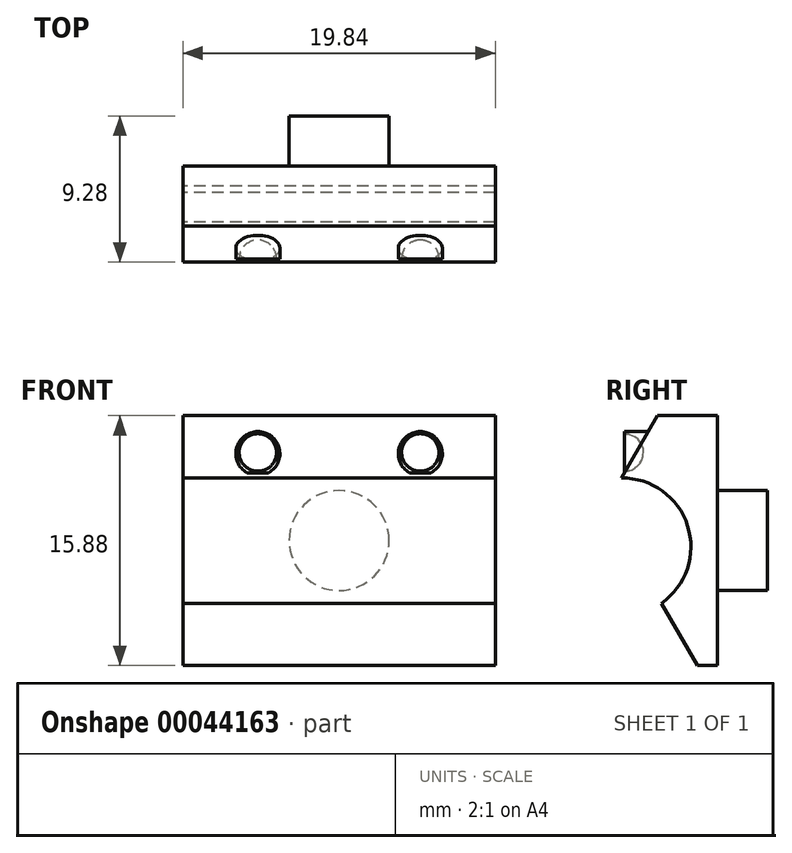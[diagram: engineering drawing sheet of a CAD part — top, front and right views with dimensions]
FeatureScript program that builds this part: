
annotation { "Feature Type Name" : "Feature", "Feature Type Description" : "" }
export const myFeature = defineFeature(function(context is Context, id is Id, definition is map)
    precondition{}
    {
        {
            var Q0;
            Q0=qCreatedBy(makeId("Right.planeOp"),FACE);
            var sketch = newSketch(context, id + "F0", { "sketchPlane" : qUnion([Q0])});
            skLineSegment(sketch, "E0", {"start": v(0, 0) * mm, "end": v(-1.27, 0) * mm});
            skLineSegment(sketch, "E1", {"start": v(-1.27, 0) * mm, "end": v(-3.56, 3.96) * mm});
            skArc(sketch, "E2", {"start": v(-3.56, 3.96) * mm, "mid": v(-1.88, 8.88) * mm, "end": v(-6.1, 11.92) * mm});
            skLineSegment(sketch, "E3", {"start": v(0, 15.88) * mm, "end": v(-3.81, 15.88) * mm});
            skLineSegment(sketch, "E4", {"start": v(-3.81, 15.88) * mm, "end": v(-6.1, 11.92) * mm});
            skLineSegment(sketch, "E5", {"start": v(0, 0) * mm, "end": v(0, 15.88) * mm});
            skSolve(sketch);
        }
        {
            var Q0;
            Q0=makeQuery(id+"F0.imprint","IMPRINT",FACE,{"disambiguationData":[TD([[makeQuery(id+"F0.imprint","IMPRINT",EDGE,{"derivedFrom":sQuery(id+"F0.wireOp",EDGE,"E0")}),-1.0]])]});
            extrude(context, id + "F1", {"entities" : qUnion([Q0]), "depth" : 19.84 * mm});
        }
        {
            var Q0;
            Q0=qCreatedBy(makeId("Front.planeOp"),FACE);
            cPlane(context, id + "F2", {"entities" : qUnion([Q0]), "cplaneType" : CPlaneType.OFFSET, "offset" : 4.32 * mm, "width" : 152.4 * mm, "height" : 152.4 * mm});
        }
        {
            var Q0;
            Q0=qCreatedBy(id+"F2.planeOp",FACE);
            var sketch = newSketch(context, id + "F3", { "sketchPlane" : qUnion([Q0])});
            skCircle(sketch, "E6", {"center": v(4.76, 13.46) * mm, "radius": 1.4 * mm});
            skCircle(sketch, "E7", {"center": v(15.08, 13.46) * mm, "radius": 1.4 * mm});
            skLineSegment(sketch, "E8", {"start": v(0, 13.46) * mm, "end": v(4.76, 13.46) * mm});
            skLineSegment(sketch, "E9", {"start": v(15.08, 13.46) * mm, "end": v(4.76, 13.46) * mm});
            skSolve(sketch);
        }
        {
            var Q0;
            Q0=makeQuery(id+"F3.imprint","IMPRINT",FACE,{"disambiguationData":[TD([[makeQuery(id+"F3.imprint","IMPRINT",EDGE,{"derivedFrom":sQuery(id+"F3.wireOp",EDGE,"E6")}),1.0]])]});
            var Q1;
            Q1=makeQuery(id+"F3.imprint","IMPRINT",FACE,{"disambiguationData":[TD([[makeQuery(id+"F3.imprint","IMPRINT",EDGE,{"derivedFrom":sQuery(id+"F3.wireOp",EDGE,"E7")}),1.0]])]});
            extrude(context, id + "F4", {"entities" : qUnion([Q0, Q1]), "operationType" : NewBodyOperationType.ADD, "depth" : 1.59 * mm});
        }
        {
            var Q0;
            Q0=qCreatedBy(makeId("Right.planeOp"),FACE);
            cPlane(context, id + "F5", {"entities" : qUnion([Q0]), "cplaneType" : CPlaneType.OFFSET, "offset" : 4.76 * mm, "width" : 152.4 * mm, "height" : 152.4 * mm});
        }
        {
            var Q0;
            Q0=qCreatedBy(id+"F5.planeOp",FACE);
            var sketch = newSketch(context, id + "F6", { "sketchPlane" : qUnion([Q0])});
            skLineSegment(sketch, "E10", {"start": v(-5.9, 12.34) * mm, "end": v(-5.9, 13.54) * mm});
            skArc(sketch, "E11", {"start": v(-5.9, 12.34) * mm, "mid": v(-4.7, 13.54) * mm, "end": v(-5.9, 14.73) * mm});
            skLineSegment(sketch, "E12", {"start": v(-5.9, 13.54) * mm, "end": v(-5.9, 14.88) * mm});
            skLineSegment(sketch, "E13", {"start": v(0, 0) * mm, "end": v(-5.9, 0) * mm});
            skLineSegment(sketch, "E14", {"start": v(-5.9, 0) * mm, "end": v(-5.9, 12.34) * mm});
            skSolve(sketch);
        }
        {
            var Q0;
            Q0 = qSketchRegion(id + "F6", true);
            var Q1;
            Q1=sQuery(id+"F6.wireOp",EDGE,"E12");
            revolve(context, id + "F7", {"operationType" : NewBodyOperationType.REMOVE, "entities" : qUnion([Q0]), "axis" : qUnion([Q1]), "revolveType" : RevolveType.FULL, "oppositeDirection" : true});
        }
        {
            var Q0;
            Q0=qCreatedBy(makeId("Right.planeOp"),FACE);
            cPlane(context, id + "F8", {"entities" : qUnion([Q0]), "cplaneType" : CPlaneType.OFFSET, "offset" : 15.08 * mm, "width" : 152.4 * mm, "height" : 152.4 * mm});
        }
        {
            var Q0;
            Q0=qCreatedBy(id+"F8.planeOp",FACE);
            var sketch = newSketch(context, id + "F9", { "sketchPlane" : qUnion([Q0])});
            skLineSegment(sketch, "E15", {"start": v(-5.9, 12.34) * mm, "end": v(-5.9, 13.54) * mm});
            skArc(sketch, "E16", {"start": v(-5.9, 12.34) * mm, "mid": v(-4.7, 13.54) * mm, "end": v(-5.9, 14.73) * mm});
            skLineSegment(sketch, "E17", {"start": v(-5.9, 13.54) * mm, "end": v(-5.9, 14.87) * mm});
            skLineSegment(sketch, "E18", {"start": v(0, 0) * mm, "end": v(-5.9, 0) * mm});
            skLineSegment(sketch, "E19", {"start": v(-5.9, 0) * mm, "end": v(-5.9, 12.34) * mm});
            skSolve(sketch);
        }
        {
            var Q0;
            Q0 = qSketchRegion(id + "F9", true);
            var Q1;
            Q1=sQuery(id+"F9.wireOp",EDGE,"E17");
            revolve(context, id + "F10", {"operationType" : NewBodyOperationType.REMOVE, "entities" : qUnion([Q0]), "axis" : qUnion([Q1]), "revolveType" : RevolveType.FULL});
        }
        {
            var Q0;
            Q0=makeQuery(id+"F1.opExtrude","SWEPT_FACE",FACE,{"disambiguationData":[OSD([sQuery(id+"F0.wireOp",EDGE,"E5")])]});
            var sketch = newSketch(context, id + "F11", { "sketchPlane" : qUnion([Q0])});
            skLineSegment(sketch, "E20", {"start": v(-9.92, 0) * mm, "end": v(-9.92, 7.94) * mm});
            skPoint(sketch, "E20.endSnap0", {"position": v(0, 7.94) * mm});
            skCircle(sketch, "E21", {"center": v(-9.92, 7.94) * mm, "radius": 3.18 * mm});
            skSolve(sketch);
        }
        {
            var Q0;
            Q0 = qSketchRegion(id + "F11", true);
            extrude(context, id + "F12", {"entities" : qUnion([Q0]), "operationType" : NewBodyOperationType.ADD, "depth" : 3.17 * mm});
        }
    });
